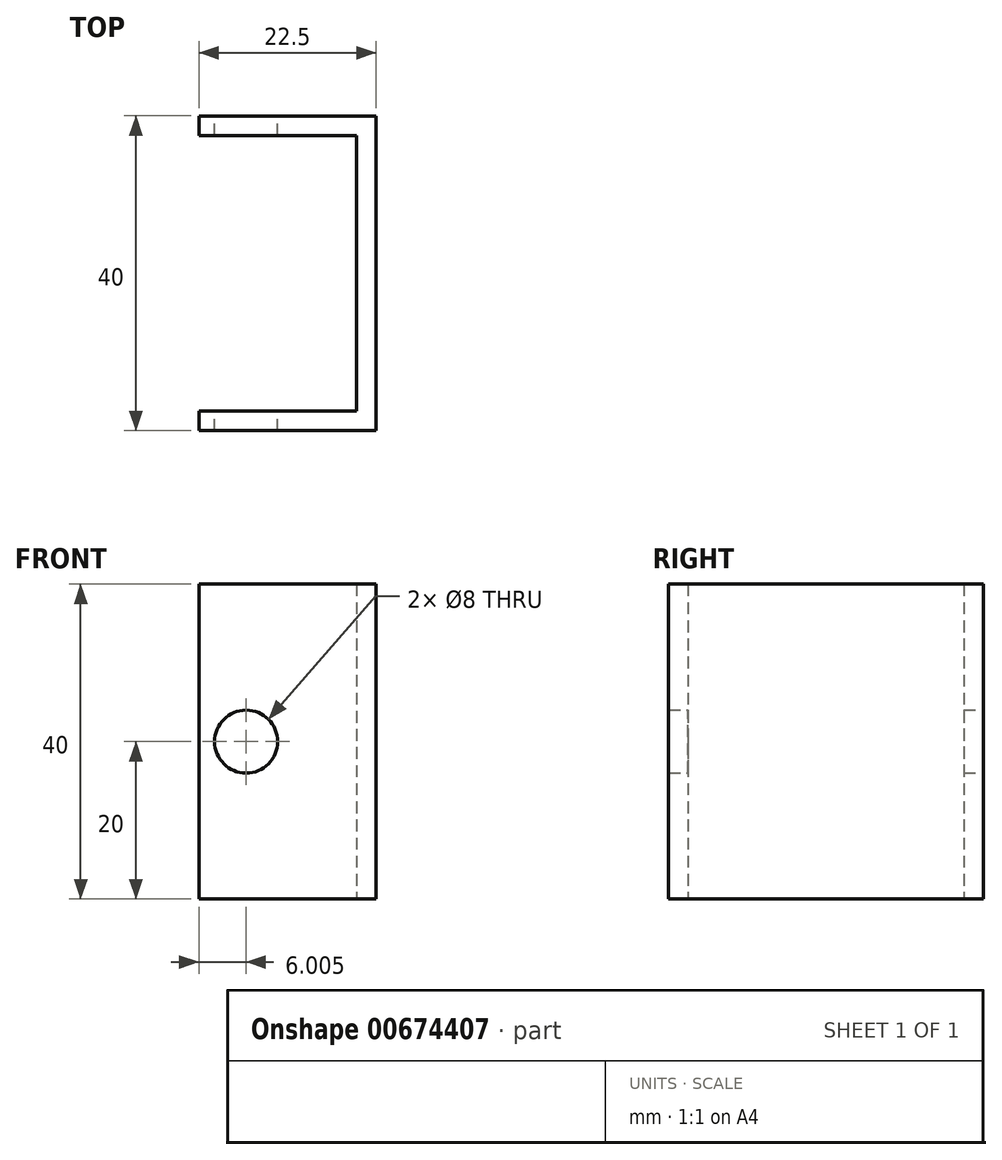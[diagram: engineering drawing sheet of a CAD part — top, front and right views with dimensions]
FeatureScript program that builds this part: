
annotation { "Feature Type Name" : "Feature", "Feature Type Description" : "" }
export const myFeature = defineFeature(function(context is Context, id is Id, definition is map)
    precondition{}
    {
        {
            var Q0;
            Q0=qCreatedBy(makeId("Top.planeOp"),FACE);
            var sketch = newSketch(context, id + "F0", { "sketchPlane" : qUnion([Q0])});
            skLineSegment(sketch, "E0", {"start": v(-15.89, -15.4) * mm, "end": v(6.61, -15.4) * mm});
            skLineSegment(sketch, "E1", {"start": v(6.61, -15.4) * mm, "end": v(6.61, 24.6) * mm});
            skLineSegment(sketch, "E2", {"start": v(6.61, 24.6) * mm, "end": v(-15.89, 24.6) * mm});
            skLineSegment(sketch, "E3", {"start": v(-15.89, 24.6) * mm, "end": v(-15.89, 22.1) * mm});
            skLineSegment(sketch, "E4", {"start": v(-15.89, 22.1) * mm, "end": v(4.11, 22.1) * mm});
            skLineSegment(sketch, "E5", {"start": v(4.11, 22.1) * mm, "end": v(4.11, -12.9) * mm});
            skLineSegment(sketch, "E6", {"start": v(4.11, -12.9) * mm, "end": v(-15.89, -12.9) * mm});
            skLineSegment(sketch, "E7", {"start": v(-15.89, -12.9) * mm, "end": v(-15.89, -15.4) * mm});
            skSolve(sketch);
        }
        {
            var Q0;
            Q0=makeQuery(id+"F0.imprint","IMPRINT",FACE,{"disambiguationData":[TD([[makeQuery(id+"F0.imprint","IMPRINT",EDGE,{"derivedFrom":sQuery(id+"F0.wireOp",EDGE,"E0")}),1.0]])]});
            extrude(context, id + "F1", {"entities" : qUnion([Q0]), "depth" : 40 * mm, "offsetDistance" : 25 * mm});
        }
        {
            var Q0;
            Q0=makeQuery(id+"F1.opExtrude","SWEPT_FACE",FACE,{"disambiguationData":[OSD([sQuery(id+"F0.wireOp",EDGE,"E2")])]});
            var sketch = newSketch(context, id + "F2", { "sketchPlane" : qUnion([Q0])});
            skCircle(sketch, "E8", {"center": v(9.89, 20) * mm, "radius": 4 * mm});
            skSolve(sketch);
        }
        {
            var Q0;
            Q0=makeQuery(id+"F2.imprint","IMPRINT",FACE,{"disambiguationData":[TD([[makeQuery(id+"F2.imprint","IMPRINT",EDGE,{"derivedFrom":sQuery(id+"F2.wireOp",EDGE,"E8")}),1.0]])]});
            extrude(context, id + "F3", {"entities" : qUnion([Q0]), "operationType" : NewBodyOperationType.REMOVE, "endBound" : BoundingType.THROUGH_ALL, "oppositeDirection" : true, "depth" : 25 * mm, "offsetDistance" : 25 * mm});
        }
    });
